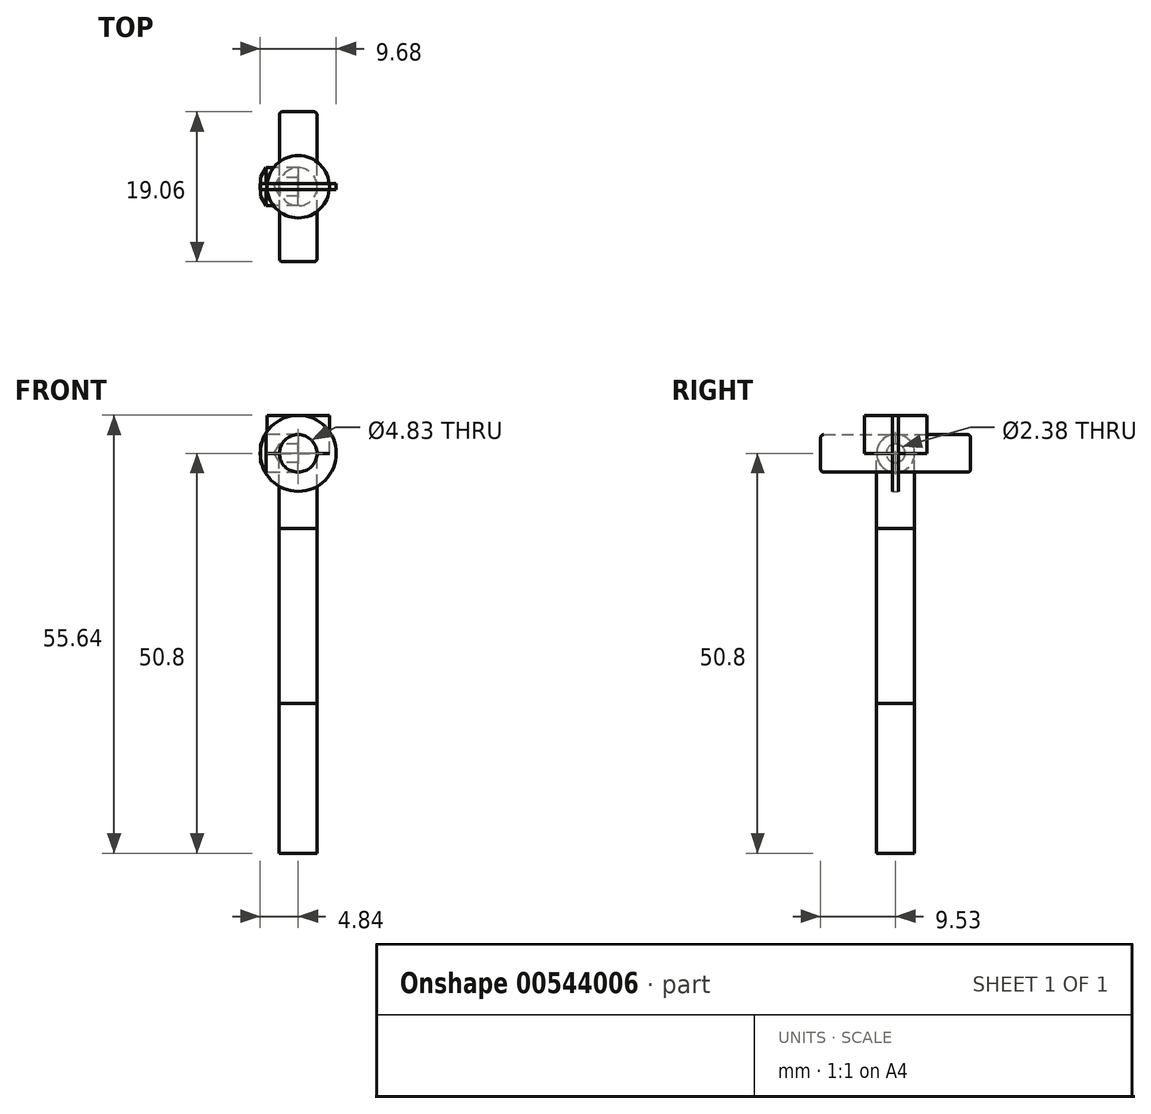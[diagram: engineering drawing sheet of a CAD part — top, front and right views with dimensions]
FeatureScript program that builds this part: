
annotation { "Feature Type Name" : "Feature", "Feature Type Description" : "" }
export const myFeature = defineFeature(function(context is Context, id is Id, definition is map)
    precondition{}
    {
        {
            var Q0;
            Q0=qCreatedBy(makeId("Front.planeOp"),FACE);
            var sketch = newSketch(context, id + "F0", { "sketchPlane" : qUnion([Q0])});
            skCircle(sketch, "E0", {"center": v(0, 0) * mm, "radius": 4.84 * mm});
            skCircle(sketch, "E1", {"center": v(0, 0) * mm, "radius": 2.41 * mm});
            skSolve(sketch);
        }
        {
            var Q0;
            Q0 = qSketchRegion(id + "F0", true);
            extrude(context, id + "F1", {"entities" : qUnion([Q0]), "depth" : 0.38 * mm, "offsetDistance" : 25.4 * mm, "hasSecondDirection" : true, "secondDirectionOppositeDirection" : true, "secondDirectionDepth" : 0.38 * mm});
        }
        {
            var Q0;
            Q0=qCreatedBy(makeId("Front.planeOp"),FACE);
            var sketch = newSketch(context, id + "F2", { "sketchPlane" : qUnion([Q0])});
            skCircle(sketch, "E2", {"center": v(0, 0) * mm, "radius": 2.38 * mm});
            skSolve(sketch);
        }
        {
            var Q0;
            Q0 = qSketchRegion(id + "F2", true);
            extrude(context, id + "F3", {"entities" : qUnion([Q0]), "depth" : 9.52 * mm, "offsetDistance" : 25.4 * mm, "hasSecondDirection" : true, "secondDirectionOppositeDirection" : true, "secondDirectionDepth" : 9.52 * mm});
        }
        {
            var Q0;
            Q0=makeQuery(id+"F3.opExtrude","CAP_EDGE",EDGE,{"disambiguationData":[OSD([sQuery(id+"F2.wireOp",EDGE,"E2")])],"isStart":false});
            var Q1;
            Q1=makeQuery(id+"F3.opExtrude","CAP_EDGE",EDGE,{"disambiguationData":[OSD([sQuery(id+"F2.wireOp",EDGE,"E2")])],"isStart":true});
            fillet(context, id + "F4", {"entities" : qUnion([Q0, Q1]), "radius" : 0.38 * mm, "tangentPropagation" : true, "allowEdgeOverflow" : false});
        }
        {
            var Q0;
            Q0=qCreatedBy(makeId("Front.planeOp"),FACE);
            var sketch = newSketch(context, id + "F5", { "sketchPlane" : qUnion([Q0])});
            skLineSegment(sketch, "E3", {"start": v(-21.95, 0) * mm, "end": v(30.43, 0) * mm, "construction": true});
            skLineSegment(sketch, "E4", {"start": v(-3.1, 0) * mm, "end": v(-2.38, 1.2) * mm});
            skLineSegment(sketch, "E5", {"start": v(-2.38, 1.2) * mm, "end": v(0, 1.2) * mm});
            skLineSegment(sketch, "E6", {"start": v(0, 1.2) * mm, "end": v(0, 2.41) * mm});
            skLineSegment(sketch, "E7", {"start": v(0, 2.41) * mm, "end": v(-4.07, 2.41) * mm});
            skLineSegment(sketch, "E8", {"start": v(-4.07, 2.41) * mm, "end": v(-4.76, 1.2) * mm});
            skLineSegment(sketch, "E9", {"start": v(-4.76, 1.2) * mm, "end": v(-4.76, 0) * mm});
            skLineSegment(sketch, "E10", {"start": v(-4.76, 0) * mm, "end": v(-3.1, 0) * mm});
            skSolve(sketch);
        }
        {
            var Q0;
            Q0 = qSketchRegion(id + "F5", true);
            var Q1;
            Q1=sQuery(id+"F5.wireOp",EDGE,"E3");
            revolve(context, id + "F6", {"entities" : qUnion([Q0]), "axis" : qUnion([Q1]), "revolveType" : RevolveType.FULL});
        }
        {
            var Q0;
            Q0=qCreatedBy(makeId("Right.planeOp"),FACE);
            var sketch = newSketch(context, id + "F7", { "sketchPlane" : qUnion([Q0])});
            skLineSegment(sketch, "E11", {"start": v(0, 4.83) * mm, "end": v(0, -9.53) * mm});
            skLineSegment(sketch, "E12", {"start": v(0, -9.53) * mm, "end": v(2.41, -9.53) * mm});
            skLineSegment(sketch, "E13", {"start": v(2.41, -9.53) * mm, "end": v(2.41, 0) * mm});
            skLineSegment(sketch, "E14", {"start": v(2.41, 0) * mm, "end": v(3.96, 0) * mm});
            skLineSegment(sketch, "E15", {"start": v(3.96, 0) * mm, "end": v(3.96, 4.83) * mm});
            skLineSegment(sketch, "E16", {"start": v(3.96, 4.83) * mm, "end": v(0, 4.83) * mm});
            skLineSegment(sketch, "E17", {"start": v(0, 8.39) * mm, "end": v(0, -14.14) * mm, "construction": true});
            skSolve(sketch);
        }
        {
            var Q0;
            Q0 = qSketchRegion(id + "F7", true);
            var Q1;
            Q1=sQuery(id+"F7.wireOp",EDGE,"E17");
            revolve(context, id + "F8", {"entities" : qUnion([Q0]), "axis" : qUnion([Q1]), "revolveType" : RevolveType.FULL});
        }
        {
            var Q0;
            Q0=qCreatedBy(makeId("Right.planeOp"),FACE);
            var sketch = newSketch(context, id + "F9", { "sketchPlane" : qUnion([Q0])});
            skLineSegment(sketch, "E18", {"start": v(0, 4.83) * mm, "end": v(0, -31.75) * mm});
            skLineSegment(sketch, "E19", {"start": v(0, -31.75) * mm, "end": v(2.41, -31.75) * mm});
            skLineSegment(sketch, "E20", {"start": v(2.41, -31.75) * mm, "end": v(2.41, 0) * mm});
            skLineSegment(sketch, "E21", {"start": v(2.41, 0) * mm, "end": v(3.96, 0) * mm});
            skLineSegment(sketch, "E22", {"start": v(3.96, 0) * mm, "end": v(3.96, 4.83) * mm});
            skLineSegment(sketch, "E23", {"start": v(3.96, 4.83) * mm, "end": v(0, 4.83) * mm});
            skLineSegment(sketch, "E24", {"start": v(0, 10.11) * mm, "end": v(0, -14.79) * mm, "construction": true});
            skSolve(sketch);
        }
        {
            var Q0;
            Q0 = qSketchRegion(id + "F9", true);
            var Q1;
            Q1=sQuery(id+"F9.wireOp",EDGE,"E24");
            revolve(context, id + "F10", {"entities" : qUnion([Q0]), "axis" : qUnion([Q1]), "revolveType" : RevolveType.FULL});
        }
        {
            var Q0;
            Q0=qCreatedBy(makeId("Right.planeOp"),FACE);
            var sketch = newSketch(context, id + "F11", { "sketchPlane" : qUnion([Q0])});
            skLineSegment(sketch, "E25", {"start": v(0, 4.83) * mm, "end": v(0, -50.8) * mm});
            skLineSegment(sketch, "E26", {"start": v(0, -50.8) * mm, "end": v(2.41, -50.8) * mm});
            skLineSegment(sketch, "E27", {"start": v(2.41, -50.8) * mm, "end": v(2.41, 0) * mm});
            skLineSegment(sketch, "E28", {"start": v(2.41, 0) * mm, "end": v(3.96, 0) * mm});
            skLineSegment(sketch, "E29", {"start": v(3.96, 0) * mm, "end": v(3.96, 4.83) * mm});
            skLineSegment(sketch, "E30", {"start": v(3.96, 4.83) * mm, "end": v(0, 4.83) * mm});
            skLineSegment(sketch, "E31", {"start": v(0, 9.33) * mm, "end": v(0, -35.63) * mm, "construction": true});
            skSolve(sketch);
        }
        {
            var Q0;
            Q0 = qSketchRegion(id + "F11", true);
            var Q1;
            Q1=sQuery(id+"F11.wireOp",EDGE,"E31");
            revolve(context, id + "F12", {"entities" : qUnion([Q0]), "axis" : qUnion([Q1]), "revolveType" : RevolveType.FULL});
        }
    });
